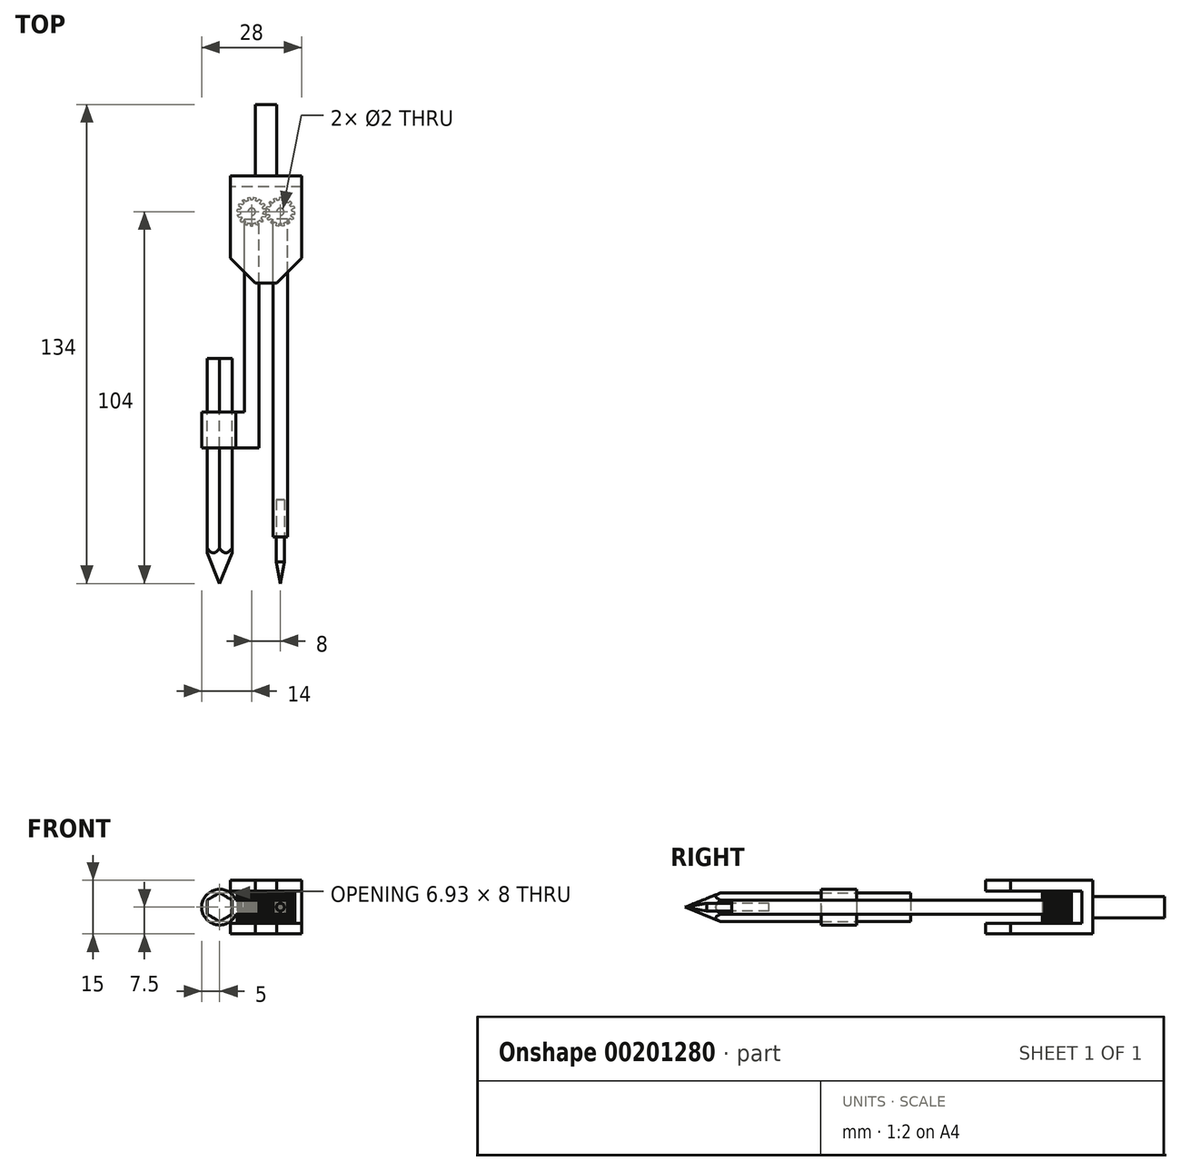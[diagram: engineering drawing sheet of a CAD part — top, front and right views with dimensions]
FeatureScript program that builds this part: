
annotation { "Feature Type Name" : "Feature", "Feature Type Description" : "" }
export const myFeature = defineFeature(function(context is Context, id is Id, definition is map)
    precondition{}
    {
        {
            var Q0;
            Q0=qCreatedBy(makeId("Top.planeOp"),FACE);
            var sketch = newSketch(context, id + "F0", { "sketchPlane" : qUnion([Q0])});
            skLineSegment(sketch, "E0.bottom", {"start": v(10, -15) * mm, "end": v(-10, -15) * mm});
            skLineSegment(sketch, "E0.top", {"start": v(10, 15) * mm, "end": v(-10, 15) * mm});
            skLineSegment(sketch, "E0.left", {"start": v(10, -15) * mm, "end": v(10, 15) * mm});
            skLineSegment(sketch, "E0.right", {"start": v(-10, -15) * mm, "end": v(-10, 15) * mm});
            skPoint(sketch, "E0.middle", {"position": v(0, 0) * mm});
            skSolve(sketch);
        }
        {
            var Q0;
            Q0=makeQuery(id+"F0.imprint","IMPRINT",FACE,{"disambiguationData":[TD([[makeQuery(id+"F0.imprint","IMPRINT",EDGE,{"derivedFrom":sQuery(id+"F0.wireOp",EDGE,"E0.bottom")}),-1.0]])]});
            extrude(context, id + "F1", {"entities" : qUnion([Q0]), "depth" : 7.5 * mm, "hasSecondDirection" : true, "secondDirectionOppositeDirection" : true, "secondDirectionDepth" : 7.5 * mm});
        }
        {
            var Q0;
            Q0=makeQuery(id+"F1.opExtrude","SWEPT_FACE",FACE,{"disambiguationData":[OSD([sQuery(id+"F0.wireOp",EDGE,"E0.bottom")])]});
            var sketch = newSketch(context, id + "F2", { "sketchPlane" : qUnion([Q0])});
            skLineSegment(sketch, "E1.bottom", {"start": v(10, -4.5) * mm, "end": v(-10, -4.5) * mm});
            skLineSegment(sketch, "E1.top", {"start": v(10, 4.5) * mm, "end": v(-10, 4.5) * mm});
            skLineSegment(sketch, "E1.left", {"start": v(10, -4.5) * mm, "end": v(10, 4.5) * mm});
            skLineSegment(sketch, "E1.right", {"start": v(-10, -4.5) * mm, "end": v(-10, 4.5) * mm});
            skPoint(sketch, "E1.middle", {"position": v(0, 0) * mm});
            skSolve(sketch);
        }
        {
            var Q0;
            Q0 = qSketchRegion(id + "F2", true);
            extrude(context, id + "F3", {"entities" : qUnion([Q0]), "operationType" : NewBodyOperationType.REMOVE, "oppositeDirection" : true, "depth" : 27 * mm});
        }
        {
            var Q0;
            Q0=makeQuery(id+"F1.opExtrude","CAP_FACE",FACE,{"disambiguationData":[OSD([sQuery(id+"F0.wireOp",EDGE,"E0.bottom"),sQuery(id+"F0.wireOp",EDGE,"E0.top"),sQuery(id+"F0.wireOp",EDGE,"E0.left"),sQuery(id+"F0.wireOp",EDGE,"E0.right")])],"isStart":false});
            var sketch = newSketch(context, id + "F4", { "sketchPlane" : qUnion([Q0])});
            skLineSegment(sketch, "E2", {"start": v(3, -15) * mm, "end": v(10, -8) * mm});
            skLineSegment(sketch, "E3", {"start": v(10, -8) * mm, "end": v(10, -15) * mm});
            skLineSegment(sketch, "E4", {"start": v(10, -15) * mm, "end": v(3, -15) * mm});
            skLineSegment(sketch, "E5.MirrorCS", {"start": v(-3, -15) * mm, "end": v(-10, -8) * mm});
            skLineSegment(sketch, "E6.MirrorCS", {"start": v(-10, -8) * mm, "end": v(-10, -15) * mm});
            skLineSegment(sketch, "E7.MirrorCS", {"start": v(-10, -15) * mm, "end": v(-3, -15) * mm});
            skSolve(sketch);
        }
        {
            var Q0;
            Q0 = qSketchRegion(id + "F4", true);
            extrude(context, id + "F5", {"entities" : qUnion([Q0]), "operationType" : NewBodyOperationType.REMOVE, "oppositeDirection" : true, "depth" : 25 * mm});
        }
        {
            var Q0;
            Q0=makeQuery(id+"F1.opExtrude","CAP_FACE",FACE,{"disambiguationData":[OSD([sQuery(id+"F0.wireOp",EDGE,"E0.bottom"),sQuery(id+"F0.wireOp",EDGE,"E0.top"),sQuery(id+"F0.wireOp",EDGE,"E0.left"),sQuery(id+"F0.wireOp",EDGE,"E0.right")])],"isStart":false});
            var sketch = newSketch(context, id + "F6", { "sketchPlane" : qUnion([Q0])});
            skCircle(sketch, "E8", {"center": v(4, 5) * mm, "radius": 1 * mm});
            skCircle(sketch, "E9.MirrorC", {"center": v(-4, 5) * mm, "radius": 1 * mm});
            skSolve(sketch);
        }
        {
            var Q0;
            Q0 = qSketchRegion(id + "F6", true);
            var Q1;
            Q1=makeQuery(id+"F3.boolean.opBoolean","COPY",FACE,{"derivedFrom":makeQuery(id+"F3.opExtrude","SWEPT_FACE",FACE,{"disambiguationData":[OSD([sQuery(id+"F2.wireOp",EDGE,"E1.bottom")])]})});
            extrude(context, id + "F7", {"entities" : qUnion([Q0]), "operationType" : NewBodyOperationType.ADD, "endBound" : BoundingType.UP_TO_SURFACE, "oppositeDirection" : true, "endBoundEntityFace" : qUnion([Q1]), "depth" : 25 * mm});
        }
        {
            var Q0;
            Q0=qCreatedBy(makeId("Top.planeOp"),FACE);
            var sketch = newSketch(context, id + "F8", { "sketchPlane" : qUnion([Q0])});
            skCircle(sketch, "E10.0", {"center": v(4, 5) * mm, "radius": 3.25 * mm});
            skLineSegment(sketch, "E11", {"start": v(4, 5) * mm, "end": v(4, 8.25) * mm, "construction": true});
            skLineSegment(sketch, "E12", {"start": v(4, 9.05) * mm, "end": v(4.3, 9.05) * mm});
            skLineSegment(sketch, "E13", {"start": v(4.3, 9.05) * mm, "end": v(4.4, 8.23) * mm});
            skLineSegment(sketch, "E14.MirrorCS", {"start": v(3.7, 9.05) * mm, "end": v(3.6, 8.23) * mm});
            skLineSegment(sketch, "E15.MirrorCS", {"start": v(4, 9.05) * mm, "end": v(3.7, 9.05) * mm});
            skLineSegment(sketch, "E16.1.0", {"start": v(2.63, 8.82) * mm, "end": v(3.05, 8.1) * mm});
            skLineSegment(sketch, "E16.1.1", {"start": v(2.35, 8.7) * mm, "end": v(2.63, 8.82) * mm});
            skLineSegment(sketch, "E16.1.2", {"start": v(2.35, 8.7) * mm, "end": v(2.08, 8.58) * mm});
            skLineSegment(sketch, "E16.1.3", {"start": v(2.08, 8.58) * mm, "end": v(2.32, 7.78) * mm});
            skLineSegment(sketch, "E16.2.0", {"start": v(1.2, 7.93) * mm, "end": v(1.87, 7.46) * mm});
            skLineSegment(sketch, "E16.2.1", {"start": v(1, 7.7) * mm, "end": v(1.2, 7.93) * mm});
            skLineSegment(sketch, "E16.2.2", {"start": v(1, 7.7) * mm, "end": v(0.79, 7.49) * mm});
            skLineSegment(sketch, "E16.2.3", {"start": v(0.79, 7.49) * mm, "end": v(1.34, 6.86) * mm});
            skLineSegment(sketch, "E16.3.0", {"start": v(0.24, 6.54) * mm, "end": v(1.06, 6.38) * mm});
            skLineSegment(sketch, "E16.3.1", {"start": v(0.15, 6.25) * mm, "end": v(0.24, 6.54) * mm});
            skLineSegment(sketch, "E16.3.2", {"start": v(0.15, 6.25) * mm, "end": v(0.06, 5.97) * mm});
            skLineSegment(sketch, "E16.3.3", {"start": v(0.06, 5.97) * mm, "end": v(0.8, 5.62) * mm});
            skLineSegment(sketch, "E16.4.0", {"start": v(-0.06, 4.88) * mm, "end": v(0.75, 5.06) * mm});
            skLineSegment(sketch, "E16.4.1", {"start": v(-0.03, 4.58) * mm, "end": v(-0.06, 4.88) * mm});
            skLineSegment(sketch, "E16.4.2", {"start": v(-0.03, 4.58) * mm, "end": v(0, 4.28) * mm});
            skLineSegment(sketch, "E16.4.3", {"start": v(0, 4.28) * mm, "end": v(0.83, 4.27) * mm});
            skLineSegment(sketch, "E16.5.0", {"start": v(0.34, 3.23) * mm, "end": v(1, 3.73) * mm});
            skLineSegment(sketch, "E16.5.1", {"start": v(0.5, 2.98) * mm, "end": v(0.34, 3.23) * mm});
            skLineSegment(sketch, "E16.5.2", {"start": v(0.5, 2.98) * mm, "end": v(0.64, 2.72) * mm});
            skLineSegment(sketch, "E16.5.3", {"start": v(0.64, 2.72) * mm, "end": v(1.4, 3.04) * mm});
            skLineSegment(sketch, "E16.6.0", {"start": v(1.38, 1.9) * mm, "end": v(1.78, 2.63) * mm});
            skLineSegment(sketch, "E16.6.1", {"start": v(1.62, 1.72) * mm, "end": v(1.38, 1.9) * mm});
            skLineSegment(sketch, "E16.6.2", {"start": v(1.62, 1.72) * mm, "end": v(1.86, 1.55) * mm});
            skLineSegment(sketch, "E16.6.3", {"start": v(1.86, 1.55) * mm, "end": v(2.43, 2.16) * mm});
            skLineSegment(sketch, "E16.7.0", {"start": v(2.86, 1.1) * mm, "end": v(2.94, 1.93) * mm});
            skLineSegment(sketch, "E16.7.1", {"start": v(3.16, 1.04) * mm, "end": v(2.86, 1.1) * mm});
            skLineSegment(sketch, "E16.7.2", {"start": v(3.16, 1.04) * mm, "end": v(3.45, 0.98) * mm});
            skLineSegment(sketch, "E16.7.3", {"start": v(3.45, 0.98) * mm, "end": v(3.72, 1.76) * mm});
            skLineSegment(sketch, "E16.8.0", {"start": v(4.55, 0.98) * mm, "end": v(4.28, 1.76) * mm});
            skLineSegment(sketch, "E16.8.1", {"start": v(4.84, 1.04) * mm, "end": v(4.55, 0.98) * mm});
            skLineSegment(sketch, "E16.8.2", {"start": v(4.84, 1.04) * mm, "end": v(5.14, 1.1) * mm});
            skLineSegment(sketch, "E16.8.3", {"start": v(5.14, 1.1) * mm, "end": v(5.06, 1.93) * mm});
            skLineSegment(sketch, "E16.9.0", {"start": v(6.14, 1.55) * mm, "end": v(5.57, 2.16) * mm});
            skLineSegment(sketch, "E16.9.1", {"start": v(6.38, 1.72) * mm, "end": v(6.14, 1.55) * mm});
            skLineSegment(sketch, "E16.9.2", {"start": v(6.38, 1.72) * mm, "end": v(6.62, 1.9) * mm});
            skLineSegment(sketch, "E16.9.3", {"start": v(6.62, 1.9) * mm, "end": v(6.22, 2.63) * mm});
            skLineSegment(sketch, "E16.10.0", {"start": v(7.36, 2.72) * mm, "end": v(6.6, 3.04) * mm});
            skLineSegment(sketch, "E16.10.1", {"start": v(7.5, 2.97) * mm, "end": v(7.36, 2.72) * mm});
            skLineSegment(sketch, "E16.10.2", {"start": v(7.5, 2.97) * mm, "end": v(7.66, 3.23) * mm});
            skLineSegment(sketch, "E16.10.3", {"start": v(7.66, 3.23) * mm, "end": v(7, 3.73) * mm});
            skLineSegment(sketch, "E16.11.0", {"start": v(8, 4.28) * mm, "end": v(7.17, 4.27) * mm});
            skLineSegment(sketch, "E16.11.1", {"start": v(8.03, 4.58) * mm, "end": v(8, 4.28) * mm});
            skLineSegment(sketch, "E16.11.2", {"start": v(8.03, 4.58) * mm, "end": v(8.06, 4.88) * mm});
            skLineSegment(sketch, "E16.11.3", {"start": v(8.06, 4.88) * mm, "end": v(7.25, 5.06) * mm});
            skLineSegment(sketch, "E16.12.0", {"start": v(7.94, 5.97) * mm, "end": v(7.2, 5.62) * mm});
            skLineSegment(sketch, "E16.12.1", {"start": v(7.85, 6.25) * mm, "end": v(7.94, 5.97) * mm});
            skLineSegment(sketch, "E16.12.2", {"start": v(7.85, 6.25) * mm, "end": v(7.76, 6.54) * mm});
            skLineSegment(sketch, "E16.12.3", {"start": v(7.76, 6.54) * mm, "end": v(6.94, 6.38) * mm});
            skLineSegment(sketch, "E16.13.0", {"start": v(7.21, 7.49) * mm, "end": v(6.66, 6.86) * mm});
            skLineSegment(sketch, "E16.13.1", {"start": v(7, 7.7) * mm, "end": v(7.21, 7.49) * mm});
            skLineSegment(sketch, "E16.13.2", {"start": v(7, 7.7) * mm, "end": v(6.8, 7.93) * mm});
            skLineSegment(sketch, "E16.13.3", {"start": v(6.8, 7.93) * mm, "end": v(6.13, 7.46) * mm});
            skLineSegment(sketch, "E16.14.0", {"start": v(5.92, 8.58) * mm, "end": v(5.68, 7.78) * mm});
            skLineSegment(sketch, "E16.14.1", {"start": v(5.65, 8.7) * mm, "end": v(5.92, 8.58) * mm});
            skLineSegment(sketch, "E16.14.2", {"start": v(5.65, 8.7) * mm, "end": v(5.37, 8.82) * mm});
            skLineSegment(sketch, "E16.14.3", {"start": v(5.37, 8.82) * mm, "end": v(4.95, 8.1) * mm});
            skCircle(sketch, "E17.0", {"center": v(4, 5) * mm, "radius": 1 * mm});
            skSolve(sketch);
        }
        {
            var Q0;
            Q0 = qSketchRegion(id + "F8", true);
            extrude(context, id + "F9", {"entities" : qUnion([Q0]), "endBound" : BoundingType.UP_TO_NEXT, "depth" : 1.8 * mm, "hasSecondDirection" : true, "secondDirectionBound" : SecondDirectionBoundingType.UP_TO_NEXT, "secondDirectionOppositeDirection" : true, "secondDirectionDepth" : 25 * mm});
        }
        {
            var Q0;
            Q0=makeQuery(id+"F9.opExtrude","SWEPT_BODY",BODY,{"disambiguationData":[OSD([sQuery(id+"F8.wireOp",EDGE,"E10.0"),sQuery(id+"F8.wireOp",EDGE,"E12"),sQuery(id+"F8.wireOp",EDGE,"E13"),sQuery(id+"F8.wireOp",EDGE,"E14.MirrorCS"),sQuery(id+"F8.wireOp",EDGE,"E15.MirrorCS"),sQuery(id+"F8.wireOp",EDGE,"E16.1.0"),sQuery(id+"F8.wireOp",EDGE,"E16.1.1"),sQuery(id+"F8.wireOp",EDGE,"E16.1.2"),sQuery(id+"F8.wireOp",EDGE,"E16.1.3"),sQuery(id+"F8.wireOp",EDGE,"E16.2.0"),sQuery(id+"F8.wireOp",EDGE,"E16.2.1"),sQuery(id+"F8.wireOp",EDGE,"E16.2.2"),sQuery(id+"F8.wireOp",EDGE,"E16.2.3"),sQuery(id+"F8.wireOp",EDGE,"E16.3.0"),sQuery(id+"F8.wireOp",EDGE,"E16.3.1"),sQuery(id+"F8.wireOp",EDGE,"E16.3.2"),sQuery(id+"F8.wireOp",EDGE,"E16.3.3"),sQuery(id+"F8.wireOp",EDGE,"E16.4.0"),sQuery(id+"F8.wireOp",EDGE,"E16.4.1"),sQuery(id+"F8.wireOp",EDGE,"E16.4.2"),sQuery(id+"F8.wireOp",EDGE,"E16.4.3"),sQuery(id+"F8.wireOp",EDGE,"E16.5.0"),sQuery(id+"F8.wireOp",EDGE,"E16.5.1"),sQuery(id+"F8.wireOp",EDGE,"E16.5.2"),sQuery(id+"F8.wireOp",EDGE,"E16.5.3"),sQuery(id+"F8.wireOp",EDGE,"E16.6.0"),sQuery(id+"F8.wireOp",EDGE,"E16.6.1"),sQuery(id+"F8.wireOp",EDGE,"E16.6.2"),sQuery(id+"F8.wireOp",EDGE,"E16.6.3"),sQuery(id+"F8.wireOp",EDGE,"E16.7.0"),sQuery(id+"F8.wireOp",EDGE,"E16.7.1"),sQuery(id+"F8.wireOp",EDGE,"E16.7.2"),sQuery(id+"F8.wireOp",EDGE,"E16.7.3"),sQuery(id+"F8.wireOp",EDGE,"E16.8.0"),sQuery(id+"F8.wireOp",EDGE,"E16.8.1"),sQuery(id+"F8.wireOp",EDGE,"E16.8.2"),sQuery(id+"F8.wireOp",EDGE,"E16.8.3"),sQuery(id+"F8.wireOp",EDGE,"E16.9.0"),sQuery(id+"F8.wireOp",EDGE,"E16.9.1"),sQuery(id+"F8.wireOp",EDGE,"E16.9.2"),sQuery(id+"F8.wireOp",EDGE,"E16.9.3"),sQuery(id+"F8.wireOp",EDGE,"E16.10.0"),sQuery(id+"F8.wireOp",EDGE,"E16.10.1"),sQuery(id+"F8.wireOp",EDGE,"E16.10.2"),sQuery(id+"F8.wireOp",EDGE,"E16.10.3"),sQuery(id+"F8.wireOp",EDGE,"E16.11.0"),sQuery(id+"F8.wireOp",EDGE,"E16.11.1"),sQuery(id+"F8.wireOp",EDGE,"E16.11.2"),sQuery(id+"F8.wireOp",EDGE,"E16.11.3"),sQuery(id+"F8.wireOp",EDGE,"E16.12.0"),sQuery(id+"F8.wireOp",EDGE,"E16.12.1"),sQuery(id+"F8.wireOp",EDGE,"E16.12.2"),sQuery(id+"F8.wireOp",EDGE,"E16.12.3"),sQuery(id+"F8.wireOp",EDGE,"E16.13.0"),sQuery(id+"F8.wireOp",EDGE,"E16.13.1"),sQuery(id+"F8.wireOp",EDGE,"E16.13.2"),sQuery(id+"F8.wireOp",EDGE,"E16.13.3"),sQuery(id+"F8.wireOp",EDGE,"E16.14.0"),sQuery(id+"F8.wireOp",EDGE,"E16.14.1"),sQuery(id+"F8.wireOp",EDGE,"E16.14.2"),sQuery(id+"F8.wireOp",EDGE,"E16.14.3"),sQuery(id+"F8.wireOp",EDGE,"E17.0")])]});
            transform(context, id + "F10", {"entities" : qUnion([Q0]), "transformType" : TransformType.TRANSLATION_3D, "dx" : -8 * mm, "dy" : 0 * mm, "dz" : 0 * mm, "makeCopy" : true});
        }
        {
            var Q0;
            Q0=makeQuery(id+"F10.opPattern","COPY",BODY,{"derivedFrom":makeQuery(id+"F9.opExtrude","SWEPT_BODY",BODY,{"disambiguationData":[OSD([sQuery(id+"F8.wireOp",EDGE,"E10.0"),sQuery(id+"F8.wireOp",EDGE,"E12"),sQuery(id+"F8.wireOp",EDGE,"E13"),sQuery(id+"F8.wireOp",EDGE,"E14.MirrorCS"),sQuery(id+"F8.wireOp",EDGE,"E15.MirrorCS"),sQuery(id+"F8.wireOp",EDGE,"E16.1.0"),sQuery(id+"F8.wireOp",EDGE,"E16.1.1"),sQuery(id+"F8.wireOp",EDGE,"E16.1.2"),sQuery(id+"F8.wireOp",EDGE,"E16.1.3"),sQuery(id+"F8.wireOp",EDGE,"E16.2.0"),sQuery(id+"F8.wireOp",EDGE,"E16.2.1"),sQuery(id+"F8.wireOp",EDGE,"E16.2.2"),sQuery(id+"F8.wireOp",EDGE,"E16.2.3"),sQuery(id+"F8.wireOp",EDGE,"E16.3.0"),sQuery(id+"F8.wireOp",EDGE,"E16.3.1"),sQuery(id+"F8.wireOp",EDGE,"E16.3.2"),sQuery(id+"F8.wireOp",EDGE,"E16.3.3"),sQuery(id+"F8.wireOp",EDGE,"E16.4.0"),sQuery(id+"F8.wireOp",EDGE,"E16.4.1"),sQuery(id+"F8.wireOp",EDGE,"E16.4.2"),sQuery(id+"F8.wireOp",EDGE,"E16.4.3"),sQuery(id+"F8.wireOp",EDGE,"E16.5.0"),sQuery(id+"F8.wireOp",EDGE,"E16.5.1"),sQuery(id+"F8.wireOp",EDGE,"E16.5.2"),sQuery(id+"F8.wireOp",EDGE,"E16.5.3"),sQuery(id+"F8.wireOp",EDGE,"E16.6.0"),sQuery(id+"F8.wireOp",EDGE,"E16.6.1"),sQuery(id+"F8.wireOp",EDGE,"E16.6.2"),sQuery(id+"F8.wireOp",EDGE,"E16.6.3"),sQuery(id+"F8.wireOp",EDGE,"E16.7.0"),sQuery(id+"F8.wireOp",EDGE,"E16.7.1"),sQuery(id+"F8.wireOp",EDGE,"E16.7.2"),sQuery(id+"F8.wireOp",EDGE,"E16.7.3"),sQuery(id+"F8.wireOp",EDGE,"E16.8.0"),sQuery(id+"F8.wireOp",EDGE,"E16.8.1"),sQuery(id+"F8.wireOp",EDGE,"E16.8.2"),sQuery(id+"F8.wireOp",EDGE,"E16.8.3"),sQuery(id+"F8.wireOp",EDGE,"E16.9.0"),sQuery(id+"F8.wireOp",EDGE,"E16.9.1"),sQuery(id+"F8.wireOp",EDGE,"E16.9.2"),sQuery(id+"F8.wireOp",EDGE,"E16.9.3"),sQuery(id+"F8.wireOp",EDGE,"E16.10.0"),sQuery(id+"F8.wireOp",EDGE,"E16.10.1"),sQuery(id+"F8.wireOp",EDGE,"E16.10.2"),sQuery(id+"F8.wireOp",EDGE,"E16.10.3"),sQuery(id+"F8.wireOp",EDGE,"E16.11.0"),sQuery(id+"F8.wireOp",EDGE,"E16.11.1"),sQuery(id+"F8.wireOp",EDGE,"E16.11.2"),sQuery(id+"F8.wireOp",EDGE,"E16.11.3"),sQuery(id+"F8.wireOp",EDGE,"E16.12.0"),sQuery(id+"F8.wireOp",EDGE,"E16.12.1"),sQuery(id+"F8.wireOp",EDGE,"E16.12.2"),sQuery(id+"F8.wireOp",EDGE,"E16.12.3"),sQuery(id+"F8.wireOp",EDGE,"E16.13.0"),sQuery(id+"F8.wireOp",EDGE,"E16.13.1"),sQuery(id+"F8.wireOp",EDGE,"E16.13.2"),sQuery(id+"F8.wireOp",EDGE,"E16.13.3"),sQuery(id+"F8.wireOp",EDGE,"E16.14.0"),sQuery(id+"F8.wireOp",EDGE,"E16.14.1"),sQuery(id+"F8.wireOp",EDGE,"E16.14.2"),sQuery(id+"F8.wireOp",EDGE,"E16.14.3"),sQuery(id+"F8.wireOp",EDGE,"E17.0")])]}),"instanceName":"1"});
            var Q1;
            Q1=makeQuery(id+"F7.boolean.opBoolean","INTERSECT",EDGE,{"derivedFrom":[makeQuery(id+"F3.boolean.opBoolean","COPY",FACE,{"derivedFrom":makeQuery(id+"F3.opExtrude","SWEPT_FACE",FACE,{"disambiguationData":[OSD([sQuery(id+"F2.wireOp",EDGE,"E1.top")])]})}),makeQuery(id+"F7.opExtrude","SWEPT_FACE",FACE,{"disambiguationData":[OSD([sQuery(id+"F6.wireOp",EDGE,"E9.MirrorC")])]})]});
            transform(context, id + "F11", {"entities" : qUnion([Q0]), "transformType" : TransformType.ROTATION, "transformAxis" : qUnion([Q1]), "angle" : 12 * degree, "makeCopy" : false});
        }
        {
            var Q0;
            Q0=qCreatedBy(makeId("Front.planeOp"),FACE);
            cPlane(context, id + "F12", {"entities" : qUnion([Q0]), "cplaneType" : CPlaneType.OFFSET, "offset" : 3 * mm, "oppositeDirection" : true, "width" : 150 * mm, "height" : 150 * mm});
        }
        {
            var Q0;
            Q0=qCreatedBy(id+"F12.planeOp",FACE);
            var sketch = newSketch(context, id + "F13", { "sketchPlane" : qUnion([Q0])});
            skLineSegment(sketch, "E18.bottom", {"start": v(6, -2) * mm, "end": v(2, -2) * mm});
            skLineSegment(sketch, "E18.top", {"start": v(6, 2) * mm, "end": v(2, 2) * mm});
            skLineSegment(sketch, "E18.left", {"start": v(6, -2) * mm, "end": v(6, 2) * mm});
            skLineSegment(sketch, "E18.right", {"start": v(2, -2) * mm, "end": v(2, 2) * mm});
            skPoint(sketch, "E18.middle", {"position": v(4, 0) * mm});
            skLineSegment(sketch, "E19.MirrorCS", {"start": v(-6, 2) * mm, "end": v(-2, 2) * mm});
            skLineSegment(sketch, "E20.MirrorCS", {"start": v(-2, -2) * mm, "end": v(-2, 2) * mm});
            skLineSegment(sketch, "E21.MirrorCS", {"start": v(-6, -2) * mm, "end": v(-6, 2) * mm});
            skLineSegment(sketch, "E22.MirrorCS", {"start": v(-6, -2) * mm, "end": v(-2, -2) * mm});
            skSolve(sketch);
        }
        {
            var Q0;
            Q0 = qSketchRegion(id + "F13", true);
            extrude(context, id + "F14", {"entities" : qUnion([Q0]), "depth" : 89 * mm});
        }
        {
            var Q0;
            Q0=qCreatedBy(makeId("Top.planeOp"),FACE);
            var sketch = newSketch(context, id + "F15", { "sketchPlane" : qUnion([Q0])});
            skLineSegment(sketch, "E23", {"start": v(4, -74) * mm, "end": v(4, -86) * mm, "construction": true});
            skLineSegment(sketch, "E24", {"start": v(4, -75.5) * mm, "end": v(5.1, -75.5) * mm});
            skLineSegment(sketch, "E25", {"start": v(5.1, -75.5) * mm, "end": v(5.1, -93) * mm});
            skLineSegment(sketch, "E26", {"start": v(5.1, -93) * mm, "end": v(4, -99) * mm});
            skLineSegment(sketch, "E27", {"start": v(4, -99) * mm, "end": v(4, -75.5) * mm});
            skSolve(sketch);
        }
        {
            var Q0;
            Q0 = qSketchRegion(id + "F15", true);
            var Q1;
            Q1=sQuery(id+"F15.wireOp",EDGE,"E27");
            revolve(context, id + "F16", {"entities" : qUnion([Q0]), "axis" : qUnion([Q1]), "revolveType" : RevolveType.FULL});
        }
        {
            var Q0;
            Q0=makeQuery(id+"F14.opExtrude","CAP_FACE",FACE,{"disambiguationData":[OSD([sQuery(id+"F13.wireOp",EDGE,"E19.MirrorCS"),sQuery(id+"F13.wireOp",EDGE,"E20.MirrorCS"),sQuery(id+"F13.wireOp",EDGE,"E21.MirrorCS"),sQuery(id+"F13.wireOp",EDGE,"E22.MirrorCS")])],"isStart":false});
            extrude(context, id + "F17", {"entities" : qUnion([Q0]), "operationType" : NewBodyOperationType.REMOVE, "oppositeDirection" : true, "depth" : 25 * mm});
        }
        {
            var Q0;
            Q0=makeQuery(id+"F14.opExtrude","SWEPT_FACE",FACE,{"disambiguationData":[OSD([sQuery(id+"F13.wireOp",EDGE,"E21.MirrorCS")])]});
            var sketch = newSketch(context, id + "F18", { "sketchPlane" : qUnion([Q0])});
            skLineSegment(sketch, "E28.bottom", {"start": v(61, 2) * mm, "end": v(51, 2) * mm});
            skLineSegment(sketch, "E28.top", {"start": v(61, -2) * mm, "end": v(51, -2) * mm});
            skLineSegment(sketch, "E28.left", {"start": v(61, 2) * mm, "end": v(61, -2) * mm});
            skLineSegment(sketch, "E28.right", {"start": v(51, 2) * mm, "end": v(51, -2) * mm});
            skSolve(sketch);
        }
        {
            var Q0;
            Q0=makeQuery(id+"F18.imprint","IMPRINT",FACE,{"disambiguationData":[TD([[makeQuery(id+"F18.imprint","IMPRINT",EDGE,{"derivedFrom":sQuery(id+"F18.wireOp",EDGE,"E28.bottom")}),1.0]])]});
            extrude(context, id + "F19", {"entities" : qUnion([Q0]), "operationType" : NewBodyOperationType.ADD, "depth" : 3 * mm});
        }
        {
            var Q0;
            Q0=makeQuery(id+"F19.boolean.opBoolean","MERGE",FACE,{"derivedFrom":[makeQuery(id+"F17.boolean.opBoolean","COPY",FACE,{"derivedFrom":makeQuery(id+"F17.opExtrude","CAP_FACE",FACE,{"disambiguationData":[OSD([sQuery(id+"F13.wireOp",EDGE,"E19.MirrorCS"),sQuery(id+"F13.wireOp",EDGE,"E20.MirrorCS"),sQuery(id+"F13.wireOp",EDGE,"E21.MirrorCS"),sQuery(id+"F13.wireOp",EDGE,"E22.MirrorCS")])],"isStart":false})}),makeQuery(id+"F19.opExtrude","SWEPT_FACE",FACE,{"disambiguationData":[OSD([sQuery(id+"F18.wireOp",EDGE,"E28.left")])]})]});
            var sketch = newSketch(context, id + "F20", { "sketchPlane" : qUnion([Q0])});
            skLineSegment(sketch, "E29", {"start": v(0, 0) * mm, "end": v(-13, 0) * mm, "construction": true});
            skPoint(sketch, "E29.endSnap0", {"position": v(-9, 0) * mm});
            skCircle(sketch, "E30", {"center": v(-13, 0) * mm, "radius": 5 * mm});
            skSolve(sketch);
        }
        {
            var Q0;
            Q0 = qSketchRegion(id + "F20", true);
            extrude(context, id + "F21", {"entities" : qUnion([Q0]), "operationType" : NewBodyOperationType.ADD, "oppositeDirection" : true, "depth" : 10 * mm});
        }
        {
            var Q0;
            Q0=makeQuery(id+"F21.boolean.opBoolean","MERGE",FACE,{"derivedFrom":[makeQuery(id+"F19.boolean.opBoolean","MERGE",FACE,{"derivedFrom":[makeQuery(id+"F17.boolean.opBoolean","COPY",FACE,{"derivedFrom":makeQuery(id+"F17.opExtrude","CAP_FACE",FACE,{"disambiguationData":[OSD([sQuery(id+"F13.wireOp",EDGE,"E19.MirrorCS"),sQuery(id+"F13.wireOp",EDGE,"E20.MirrorCS"),sQuery(id+"F13.wireOp",EDGE,"E21.MirrorCS"),sQuery(id+"F13.wireOp",EDGE,"E22.MirrorCS")])],"isStart":false})}),makeQuery(id+"F19.opExtrude","SWEPT_FACE",FACE,{"disambiguationData":[OSD([sQuery(id+"F18.wireOp",EDGE,"E28.left")])]})]}),makeQuery(id+"F21.opExtrude","CAP_FACE",FACE,{"disambiguationData":[OSD([sQuery(id+"F20.wireOp",EDGE,"E30")])],"isStart":true})]});
            var sketch = newSketch(context, id + "F22", { "sketchPlane" : qUnion([Q0])});
            skCircle(sketch, "E31.cCircle", {"center": v(-13, 0) * mm, "radius": 3.46 * mm, "construction": true});
            skLineSegment(sketch, "E31.0", {"start": v(-16.46, 2) * mm, "end": v(-13, 4) * mm});
            skLineSegment(sketch, "E31.1", {"start": v(-13, 4) * mm, "end": v(-9.54, 2) * mm});
            skLineSegment(sketch, "E31.2", {"start": v(-9.54, 2) * mm, "end": v(-9.54, -2) * mm});
            skLineSegment(sketch, "E31.3", {"start": v(-9.54, -2) * mm, "end": v(-13, -4) * mm});
            skLineSegment(sketch, "E31.4", {"start": v(-13, -4) * mm, "end": v(-16.46, -2) * mm});
            skLineSegment(sketch, "E31.5", {"start": v(-16.46, -2) * mm, "end": v(-16.46, 2) * mm});
            skPoint(sketch, "E31.0.midPoint", {"position": v(-14.73, 3) * mm});
            skSolve(sketch);
        }
        {
            var Q0;
            Q0 = qSketchRegion(id + "F22", true);
            extrude(context, id + "F23", {"entities" : qUnion([Q0]), "operationType" : NewBodyOperationType.REMOVE, "endBound" : BoundingType.UP_TO_NEXT, "oppositeDirection" : true, "depth" : 25 * mm});
        }
        {
            var Q0;
            Q0=makeQuery(id+"F21.boolean.opBoolean","MERGE",FACE,{"derivedFrom":[makeQuery(id+"F19.boolean.opBoolean","MERGE",FACE,{"derivedFrom":[makeQuery(id+"F17.boolean.opBoolean","COPY",FACE,{"derivedFrom":makeQuery(id+"F17.opExtrude","CAP_FACE",FACE,{"disambiguationData":[OSD([sQuery(id+"F13.wireOp",EDGE,"E19.MirrorCS"),sQuery(id+"F13.wireOp",EDGE,"E20.MirrorCS"),sQuery(id+"F13.wireOp",EDGE,"E21.MirrorCS"),sQuery(id+"F13.wireOp",EDGE,"E22.MirrorCS")])],"isStart":false})}),makeQuery(id+"F19.opExtrude","SWEPT_FACE",FACE,{"disambiguationData":[OSD([sQuery(id+"F18.wireOp",EDGE,"E28.left")])]})]}),makeQuery(id+"F21.opExtrude","CAP_FACE",FACE,{"disambiguationData":[OSD([sQuery(id+"F20.wireOp",EDGE,"E30")])],"isStart":true})]});
            var sketch = newSketch(context, id + "F24", { "sketchPlane" : qUnion([Q0])});
            skLineSegment(sketch, "E32.0", {"start": v(-13, 4) * mm, "end": v(-9.54, 2) * mm});
            skLineSegment(sketch, "E33.0", {"start": v(-16.46, 2) * mm, "end": v(-13, 4) * mm});
            skLineSegment(sketch, "E34.0", {"start": v(-16.46, -2) * mm, "end": v(-16.46, 2) * mm});
            skLineSegment(sketch, "E35.0", {"start": v(-13, -4) * mm, "end": v(-16.46, -2) * mm});
            skLineSegment(sketch, "E36.0", {"start": v(-9.54, -2) * mm, "end": v(-13, -4) * mm});
            skLineSegment(sketch, "E37.0", {"start": v(-9.54, 2) * mm, "end": v(-9.54, -2) * mm});
            skSolve(sketch);
        }
        {
            var Q0;
            Q0 = qSketchRegion(id + "F24", true);
            var Q1;
            Q1=makeQuery(id+"F16.opRevolve","SWEPT_VERTEX",VERTEX,{"disambiguationData":[OSD([sQuery(id+"F15.wireOp",EDGE,"E26"),sQuery(id+"F15.wireOp",EDGE,"E27")])]});
            extrude(context, id + "F25", {"entities" : qUnion([Q0]), "endBound" : BoundingType.UP_TO_VERTEX, "endBoundEntityVertex" : qUnion([Q1]), "depth" : 39.1 * mm, "hasSecondDirection" : true, "secondDirectionOppositeDirection" : true, "secondDirectionDepth" : 25 * mm});
        }
        {
            var Q0;
            Q0=qCreatedBy(makeId("Top.planeOp"),FACE);
            var sketch = newSketch(context, id + "F26", { "sketchPlane" : qUnion([Q0])});
            skLineSegment(sketch, "E38", {"start": v(-13, -99) * mm, "end": v(-13, 0) * mm});
            skLineSegment(sketch, "E39", {"start": v(-13, 0) * mm, "end": v(-53, 0) * mm});
            skLineSegment(sketch, "E40", {"start": v(-53, 0) * mm, "end": v(-13, -99) * mm});
            skSolve(sketch);
        }
        {
            var Q0;
            Q0 = qSketchRegion(id + "F26", true);
            var Q1;
            Q1=sQuery(id+"F26.wireOp",EDGE,"E38");
            revolve(context, id + "F27", {"entities" : qUnion([Q0]), "axis" : qUnion([Q1]), "revolveType" : RevolveType.FULL});
        }
        {
            var Q0;
            Q0=makeQuery(id+"F27.opRevolve","SWEPT_BODY",BODY,{"disambiguationData":[OSD([sQuery(id+"F26.wireOp",EDGE,"E38"),sQuery(id+"F26.wireOp",EDGE,"E39"),sQuery(id+"F26.wireOp",EDGE,"E40")])]});
            var Q1;
            Q1=makeQuery(id+"F25.opExtrude","SWEPT_BODY",BODY,{"disambiguationData":[OSD([sQuery(id+"F24.wireOp",EDGE,"E32.0"),sQuery(id+"F24.wireOp",EDGE,"E33.0"),sQuery(id+"F24.wireOp",EDGE,"E34.0"),sQuery(id+"F24.wireOp",EDGE,"E35.0"),sQuery(id+"F24.wireOp",EDGE,"E36.0"),sQuery(id+"F24.wireOp",EDGE,"E37.0")])]});
            booleanBodies(context, id + "F28", {"operationType" : BooleanOperationType.INTERSECTION, "tools" : qUnion([Q0, Q1])});
        }
        {
            var Q0;
            Q0=makeQuery(id+"F1.opExtrude","SWEPT_FACE",FACE,{"disambiguationData":[OSD([sQuery(id+"F0.wireOp",EDGE,"E0.top")])]});
            var sketch = newSketch(context, id + "F29", { "sketchPlane" : qUnion([Q0])});
            skCircle(sketch, "E41", {"center": v(0, 0) * mm, "radius": 3 * mm});
            skSolve(sketch);
        }
        {
            var Q0;
            Q0 = qSketchRegion(id + "F29", true);
            extrude(context, id + "F30", {"entities" : qUnion([Q0]), "operationType" : NewBodyOperationType.ADD, "depth" : 20 * mm});
        }
        {
            var Q0;
            Q0=makeQuery(id+"F16.opRevolve","SWEPT_BODY",BODY,{"disambiguationData":[OSD([sQuery(id+"F15.wireOp",EDGE,"E24"),sQuery(id+"F15.wireOp",EDGE,"E25"),sQuery(id+"F15.wireOp",EDGE,"E26"),sQuery(id+"F15.wireOp",EDGE,"E27")])]});
            var Q1;
            Q1=makeQuery(id+"F9.opExtrude","SWEPT_BODY",BODY,{"disambiguationData":[OSD([sQuery(id+"F8.wireOp",EDGE,"E10.0"),sQuery(id+"F8.wireOp",EDGE,"E12"),sQuery(id+"F8.wireOp",EDGE,"E13"),sQuery(id+"F8.wireOp",EDGE,"E14.MirrorCS"),sQuery(id+"F8.wireOp",EDGE,"E15.MirrorCS"),sQuery(id+"F8.wireOp",EDGE,"E16.1.0"),sQuery(id+"F8.wireOp",EDGE,"E16.1.1"),sQuery(id+"F8.wireOp",EDGE,"E16.1.2"),sQuery(id+"F8.wireOp",EDGE,"E16.1.3"),sQuery(id+"F8.wireOp",EDGE,"E16.2.0"),sQuery(id+"F8.wireOp",EDGE,"E16.2.1"),sQuery(id+"F8.wireOp",EDGE,"E16.2.2"),sQuery(id+"F8.wireOp",EDGE,"E16.2.3"),sQuery(id+"F8.wireOp",EDGE,"E16.3.0"),sQuery(id+"F8.wireOp",EDGE,"E16.3.1"),sQuery(id+"F8.wireOp",EDGE,"E16.3.2"),sQuery(id+"F8.wireOp",EDGE,"E16.3.3"),sQuery(id+"F8.wireOp",EDGE,"E16.4.0"),sQuery(id+"F8.wireOp",EDGE,"E16.4.1"),sQuery(id+"F8.wireOp",EDGE,"E16.4.2"),sQuery(id+"F8.wireOp",EDGE,"E16.4.3"),sQuery(id+"F8.wireOp",EDGE,"E16.5.0"),sQuery(id+"F8.wireOp",EDGE,"E16.5.1"),sQuery(id+"F8.wireOp",EDGE,"E16.5.2"),sQuery(id+"F8.wireOp",EDGE,"E16.5.3"),sQuery(id+"F8.wireOp",EDGE,"E16.6.0"),sQuery(id+"F8.wireOp",EDGE,"E16.6.1"),sQuery(id+"F8.wireOp",EDGE,"E16.6.2"),sQuery(id+"F8.wireOp",EDGE,"E16.6.3"),sQuery(id+"F8.wireOp",EDGE,"E16.7.0"),sQuery(id+"F8.wireOp",EDGE,"E16.7.1"),sQuery(id+"F8.wireOp",EDGE,"E16.7.2"),sQuery(id+"F8.wireOp",EDGE,"E16.7.3"),sQuery(id+"F8.wireOp",EDGE,"E16.8.0"),sQuery(id+"F8.wireOp",EDGE,"E16.8.1"),sQuery(id+"F8.wireOp",EDGE,"E16.8.2"),sQuery(id+"F8.wireOp",EDGE,"E16.8.3"),sQuery(id+"F8.wireOp",EDGE,"E16.9.0"),sQuery(id+"F8.wireOp",EDGE,"E16.9.1"),sQuery(id+"F8.wireOp",EDGE,"E16.9.2"),sQuery(id+"F8.wireOp",EDGE,"E16.9.3"),sQuery(id+"F8.wireOp",EDGE,"E16.10.0"),sQuery(id+"F8.wireOp",EDGE,"E16.10.1"),sQuery(id+"F8.wireOp",EDGE,"E16.10.2"),sQuery(id+"F8.wireOp",EDGE,"E16.10.3"),sQuery(id+"F8.wireOp",EDGE,"E16.11.0"),sQuery(id+"F8.wireOp",EDGE,"E16.11.1"),sQuery(id+"F8.wireOp",EDGE,"E16.11.2"),sQuery(id+"F8.wireOp",EDGE,"E16.11.3"),sQuery(id+"F8.wireOp",EDGE,"E16.12.0"),sQuery(id+"F8.wireOp",EDGE,"E16.12.1"),sQuery(id+"F8.wireOp",EDGE,"E16.12.2"),sQuery(id+"F8.wireOp",EDGE,"E16.12.3"),sQuery(id+"F8.wireOp",EDGE,"E16.13.0"),sQuery(id+"F8.wireOp",EDGE,"E16.13.1"),sQuery(id+"F8.wireOp",EDGE,"E16.13.2"),sQuery(id+"F8.wireOp",EDGE,"E16.13.3"),sQuery(id+"F8.wireOp",EDGE,"E16.14.0"),sQuery(id+"F8.wireOp",EDGE,"E16.14.1"),sQuery(id+"F8.wireOp",EDGE,"E16.14.2"),sQuery(id+"F8.wireOp",EDGE,"E16.14.3"),sQuery(id+"F8.wireOp",EDGE,"E17.0")])]});
            booleanBodies(context, id + "F31", {"operationType" : BooleanOperationType.SUBTRACTION, "tools" : qUnion([Q0]), "targets" : qUnion([Q1]), "keepTools" : true});
        }
    });
